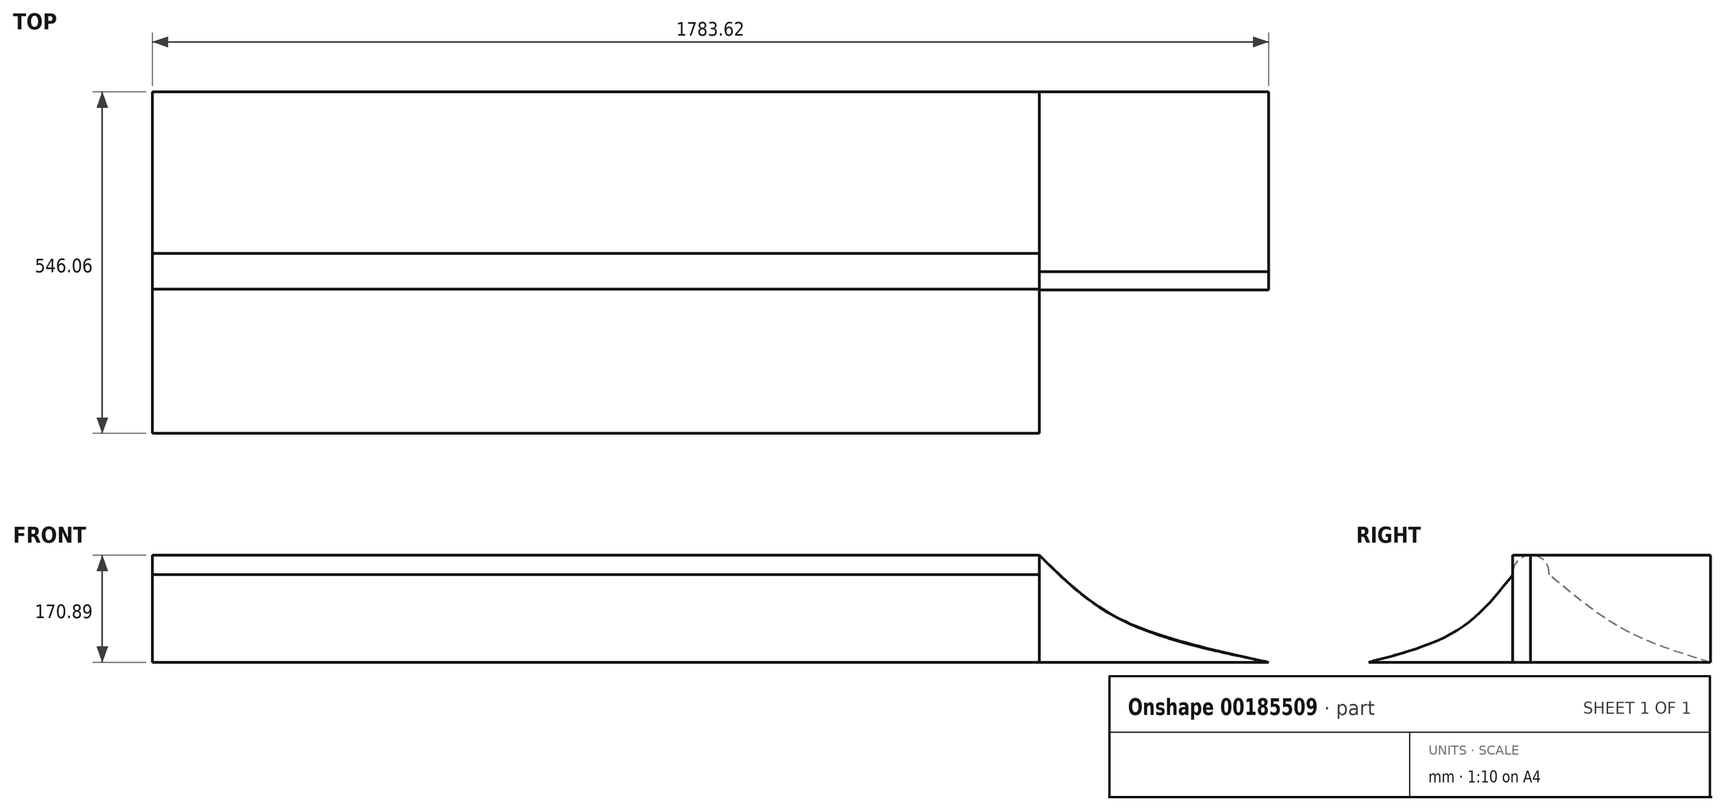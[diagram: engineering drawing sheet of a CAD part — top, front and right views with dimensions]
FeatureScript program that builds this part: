
annotation { "Feature Type Name" : "Feature", "Feature Type Description" : "" }
export const myFeature = defineFeature(function(context is Context, id is Id, definition is map)
    precondition{}
    {
        {
            var Q0;
            Q0=qCreatedBy(makeId("Front.planeOp"),FACE);
            var sketch = newSketch(context, id + "F0", { "sketchPlane" : qUnion([Q0])});
            skLineSegment(sketch, "E0", {"start": v(952.66, -170.9) * mm, "end": v(586, -170.9) * mm});
            skLineSegment(sketch, "E1", {"start": v(586, -170.9) * mm, "end": v(586, 0) * mm});
            skFitSpline(sketch, "E2", {"points": [v(586, 0) * mm, v(704.98, -96.78) * mm, v(952.66, -170.9) * mm], "startDerivative": vector(237.53, -242.3) * mm, "endDerivative": vector(485.06, -105.42) * mm});
            skSolve(sketch);
        }
        {
            var Q0;
            Q0 = qSketchRegion(id + "F0", true);
            extrude(context, id + "F1", {"entities" : qUnion([Q0]), "oppositeDirection" : true, "depth" : 287.65 * mm});
        }
        {
            var Q0;
            Q0=makeQuery(id+"F1.opExtrude","SWEPT_FACE",FACE,{"disambiguationData":[OSD([sQuery(id+"F0.wireOp",EDGE,"E1")])]});
            var sketch = newSketch(context, id + "F2", { "sketchPlane" : qUnion([Q0])});
            skLineSegment(sketch, "E3", {"start": v(0, -170.9) * mm, "end": v(-287.65, -170.9) * mm});
            skFitSpline(sketch, "E4", {"points": [v(-287.65, -170.9) * mm, v(-149.36, -118.56) * mm, v(-29.78, -30.6) * mm], "startDerivative": vector(286.32, 87.04) * mm, "endDerivative": vector(229.44, 193.53) * mm});
            skLineSegment(sketch, "E5", {"start": v(-29.78, -30.6) * mm, "end": v(-29.78, 0) * mm});
            skLineSegment(sketch, "E6", {"start": v(-29.78, 0) * mm, "end": v(27.95, 0) * mm});
            skLineSegment(sketch, "E7", {"start": v(27.95, 0) * mm, "end": v(27.95, -30.6) * mm});
            skFitSpline(sketch, "E8", {"points": [v(27.95, -30.6) * mm, v(115.02, -118.56) * mm, v(258.4, -170.9) * mm], "startDerivative": vector(162.73, -206.1) * mm, "endDerivative": vector(295.86, -76.77) * mm});
            skLineSegment(sketch, "E9", {"start": v(258.4, -170.9) * mm, "end": v(0, -170.9) * mm});
            skSolve(sketch);
        }
        {
            var Q0;
            Q0 = qSketchRegion(id + "F2", true);
            extrude(context, id + "F3", {"entities" : qUnion([Q0]), "operationType" : NewBodyOperationType.ADD, "depth" : 1416.97 * mm});
        }
        {
            var Q0;
            Q0=makeQuery(id+"F3.opExtrude","SWEPT_EDGE",EDGE,{"disambiguationData":[OSD([sQuery(id+"F2.wireOp",EDGE,"E6"),sQuery(id+"F2.wireOp",EDGE,"E7")])]});
            var Q1;
            Q1=makeQuery(id+"F3.opExtrude","SWEPT_EDGE",EDGE,{"disambiguationData":[OSD([sQuery(id+"F0.wireOp",EDGE,"E1"),sQuery(id+"F0.wireOp",EDGE,"E2"),sQuery(id+"F2.wireOp",EDGE,"E5"),sQuery(id+"F2.wireOp",EDGE,"E6")])]});
            fillet(context, id + "F4", {"entities" : qUnion([Q0, Q1]), "radius" : 27.94 * mm, "tangentPropagation" : true, "allowEdgeOverflow" : false});
        }
        {
            var Q0;
            Q0=makeQuery(id+"F1.opExtrude","CAP_FACE",FACE,{"disambiguationData":[OSD([sQuery(id+"F0.wireOp",EDGE,"E0"),sQuery(id+"F0.wireOp",EDGE,"E1"),sQuery(id+"F0.wireOp",EDGE,"E2")])],"isStart":true});
            var sketch = newSketch(context, id + "F5", { "sketchPlane" : qUnion([Q0])});
            skLineSegment(sketch, "E10", {"start": v(952.66, -170.9) * mm, "end": v(586, -170.9) * mm});
            skLineSegment(sketch, "E11", {"start": v(586, -170.9) * mm, "end": v(586, 0) * mm});
            skFitSpline(sketch, "E12", {"points": [v(586, 0) * mm, v(715.32, -102.03) * mm, v(952.66, -170.9) * mm], "startDerivative": vector(256.3, -248.35) * mm, "endDerivative": vector(469.8, -98.5) * mm});
            skSolve(sketch);
        }
        {
            var Q0;
            Q0 = qSketchRegion(id + "F5", true);
            extrude(context, id + "F6", {"entities" : qUnion([Q0]), "operationType" : NewBodyOperationType.ADD, "depth" : 28.67 * mm});
        }
    });
